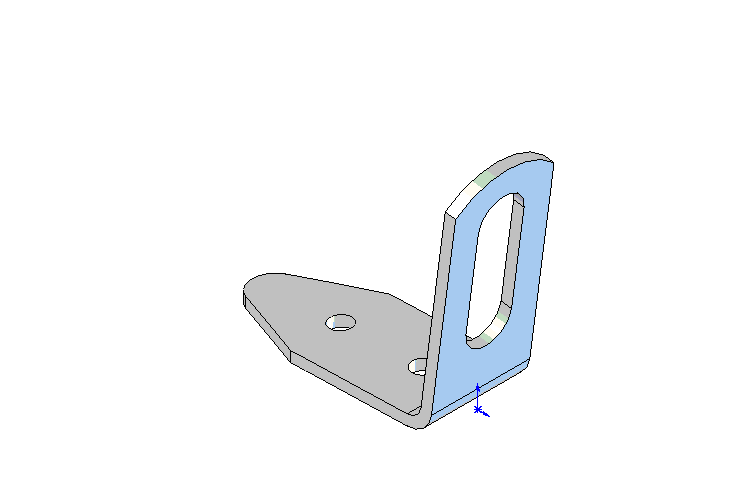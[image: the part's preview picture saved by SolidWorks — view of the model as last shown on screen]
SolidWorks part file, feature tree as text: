
SOLIDWORKS PART (.sldprt)
format: sldprt  version: not decoded by parser v0  size: 270,336 bytes
history: native  units: mm
features: sketch x5, plane x3, cut_extrude x2, cut_revolve x2, material x1, extrude x1 (+10 scaffold rows collapsed)
feature tree (24):
  scaffold x10  (default folders/planes/origin — collapsed)
  material  "Matériau <non spécifié>"
  plane  "Plan de face"
  plane  "Plan de dessus"
  plane  "Plan de droite"
  sketch  "Esquisse1"  dims[c1.D5=371.5mm c1.D6=2.0mm c1.D7=3.5mm c1.D1=~35.028414mm c2.D1=30.0deg c2.D3=32.0mm c2.D4=32.0mm c2.D2=1.5mm c3.D4=32.0mm c3.D1=~25.98558mm c4.D1=97.6deg c4.D2=1.5mm]
  extrude  "Extrusion1"  Depth=14mm
  sketch  "Esquisse2"  dims[c1.D2=3.25mm c1.D3=3.25mm c1.D4=10.0mm c1.D1=6.5mm c2.D2=3.5mm c2.D3=20.0mm]
  cut_extrude  "Enlèv. mat.-Extru.1"  [1 undecoded]
  sketch  "Esquisse3"  dims[c1.D1=6.0mm c1.D3=3.0mm c1.D5=3.0mm c1.D2=12.5mm c1.D4=11.5mm c2.D5=13.0mm]
  cut_extrude  "Enlèv. mat.-Extru.2"  [1 undecoded]
  sketch  "Esquisse4"  dims[c1.D1=3.0mm c1.D2=~401.827075mm c2.D2=10.6deg]
  cut_revolve  "Enlèvement de matière-Révolution1"  Angle=360deg
  sketch  "Esquisse5"  dims[c1.D1=~381.677693mm c2.D1=1.8deg c2.D2=3.0mm]
  cut_revolve  "Enlèvement de matière-Révolution2"  Angle=360deg
decode coverage: 8 of 10 modeling features carry decoded parameters
note: ~ marks probable driven/reference dimensions
note: 2 parameter values undecoded
note: suppression state not decoded; provenance and decode notes live in map.json
